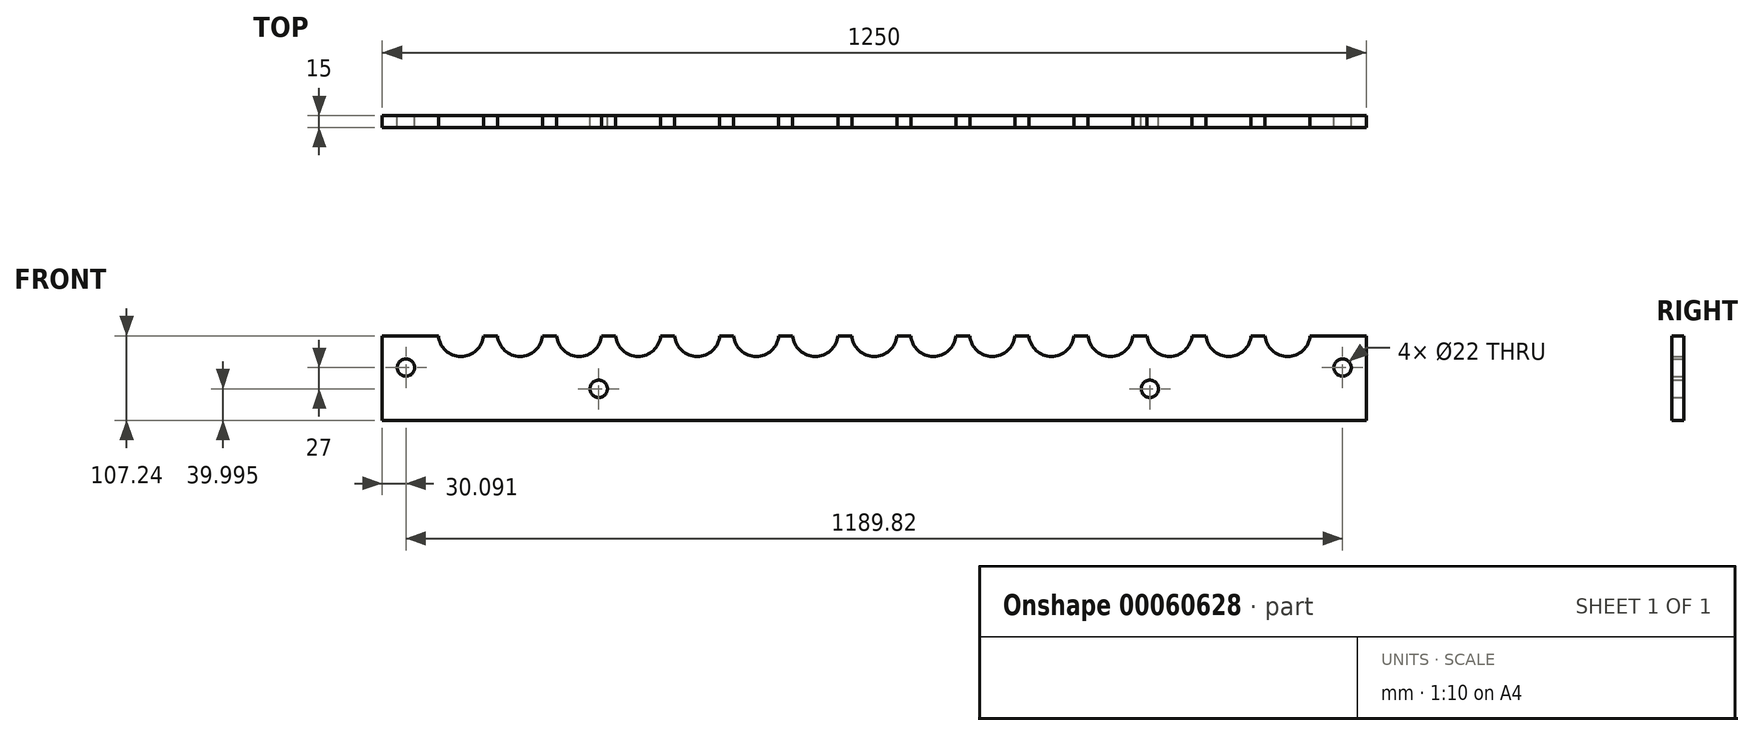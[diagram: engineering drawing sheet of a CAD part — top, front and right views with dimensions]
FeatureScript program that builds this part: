
annotation { "Feature Type Name" : "Feature", "Feature Type Description" : "" }
export const myFeature = defineFeature(function(context is Context, id is Id, definition is map)
    precondition{}
    {
        {
            var Q0;
            Q0=qCreatedBy(makeId("Front.planeOp"),FACE);
            var sketch = newSketch(context, id + "F0", { "sketchPlane" : qUnion([Q0])});
            skCircle(sketch, "E0", {"center": v(-594.9, 13.38) * mm, "radius": 11 * mm});
            skCircle(sketch, "E1", {"center": v(594.9, 13.38) * mm, "radius": 11 * mm});
            skCircle(sketch, "E2", {"center": v(350, -13.62) * mm, "radius": 11 * mm});
            skCircle(sketch, "E3", {"center": v(-350, -13.62) * mm, "radius": 11 * mm});
            skLineSegment(sketch, "E4", {"start": v(625, 53.62) * mm, "end": v(625, -53.62) * mm});
            skLineSegment(sketch, "E5", {"start": v(625, -53.62) * mm, "end": v(-625, -53.62) * mm});
            skLineSegment(sketch, "E6", {"start": v(-625, -53.62) * mm, "end": v(-625, 53.62) * mm});
            skLineSegment(sketch, "E7", {"start": v(625, 53.62) * mm, "end": v(553.62, 53.62) * mm});
            skLineSegment(sketch, "E8", {"start": v(496.38, 53.62) * mm, "end": v(478.62, 53.62) * mm});
            skLineSegment(sketch, "E9", {"start": v(421.38, 53.62) * mm, "end": v(403.62, 53.62) * mm});
            skLineSegment(sketch, "E10", {"start": v(346.38, 53.62) * mm, "end": v(328.62, 53.62) * mm});
            skLineSegment(sketch, "E11", {"start": v(271.38, 53.62) * mm, "end": v(253.62, 53.62) * mm});
            skLineSegment(sketch, "E12", {"start": v(196.38, 53.62) * mm, "end": v(178.62, 53.62) * mm});
            skLineSegment(sketch, "E13", {"start": v(121.38, 53.62) * mm, "end": v(103.62, 53.62) * mm});
            skLineSegment(sketch, "E14", {"start": v(46.38, 53.62) * mm, "end": v(28.62, 53.62) * mm});
            skLineSegment(sketch, "E15", {"start": v(-28.62, 53.62) * mm, "end": v(-46.38, 53.62) * mm});
            skLineSegment(sketch, "E16", {"start": v(-103.62, 53.62) * mm, "end": v(-121.38, 53.62) * mm});
            skLineSegment(sketch, "E17", {"start": v(-178.62, 53.62) * mm, "end": v(-196.38, 53.62) * mm});
            skLineSegment(sketch, "E18", {"start": v(-253.62, 53.62) * mm, "end": v(-271.38, 53.62) * mm});
            skLineSegment(sketch, "E19", {"start": v(-328.62, 53.62) * mm, "end": v(-346.38, 53.62) * mm});
            skLineSegment(sketch, "E20", {"start": v(-403.62, 53.62) * mm, "end": v(-421.38, 53.62) * mm});
            skLineSegment(sketch, "E21", {"start": v(-478.62, 53.62) * mm, "end": v(-496.38, 53.62) * mm});
            skLineSegment(sketch, "E22", {"start": v(-553.62, 53.62) * mm, "end": v(-625, 53.62) * mm});
            skArc(sketch, "E23", {"start": v(-553.62, 53.62) * mm, "mid": v(-525, 27.62) * mm, "end": v(-496.38, 53.62) * mm});
            skArc(sketch, "E24", {"start": v(-478.62, 53.62) * mm, "mid": v(-450, 27.62) * mm, "end": v(-421.38, 53.62) * mm});
            skArc(sketch, "E25", {"start": v(-403.62, 53.62) * mm, "mid": v(-375, 27.62) * mm, "end": v(-346.38, 53.62) * mm});
            skArc(sketch, "E26", {"start": v(-328.62, 53.62) * mm, "mid": v(-300, 27.62) * mm, "end": v(-271.38, 53.62) * mm});
            skArc(sketch, "E27", {"start": v(-253.62, 53.62) * mm, "mid": v(-225, 27.62) * mm, "end": v(-196.38, 53.62) * mm});
            skArc(sketch, "E28", {"start": v(-178.62, 53.62) * mm, "mid": v(-150, 27.62) * mm, "end": v(-121.38, 53.62) * mm});
            skArc(sketch, "E29", {"start": v(-103.62, 53.62) * mm, "mid": v(-75, 27.62) * mm, "end": v(-46.38, 53.62) * mm});
            skArc(sketch, "E30", {"start": v(-28.62, 53.62) * mm, "mid": v(0, 27.62) * mm, "end": v(28.62, 53.62) * mm});
            skArc(sketch, "E31", {"start": v(46.38, 53.62) * mm, "mid": v(75, 27.62) * mm, "end": v(103.62, 53.62) * mm});
            skArc(sketch, "E32", {"start": v(121.38, 53.62) * mm, "mid": v(150, 27.62) * mm, "end": v(178.62, 53.62) * mm});
            skArc(sketch, "E33", {"start": v(196.38, 53.62) * mm, "mid": v(225, 27.62) * mm, "end": v(253.62, 53.62) * mm});
            skArc(sketch, "E34", {"start": v(271.38, 53.62) * mm, "mid": v(300, 27.62) * mm, "end": v(328.62, 53.62) * mm});
            skArc(sketch, "E35", {"start": v(346.38, 53.62) * mm, "mid": v(375, 27.62) * mm, "end": v(403.62, 53.62) * mm});
            skArc(sketch, "E36", {"start": v(421.38, 53.62) * mm, "mid": v(450, 27.62) * mm, "end": v(478.62, 53.62) * mm});
            skArc(sketch, "E37", {"start": v(496.38, 53.62) * mm, "mid": v(525, 27.62) * mm, "end": v(553.62, 53.62) * mm});
            skSolve(sketch);
        }
        {
            var Q0;
            Q0 = qSketchRegion(id + "F0", true);
            extrude(context, id + "F1", {"entities" : qUnion([Q0]), "depth" : 15 * mm});
        }
    });
